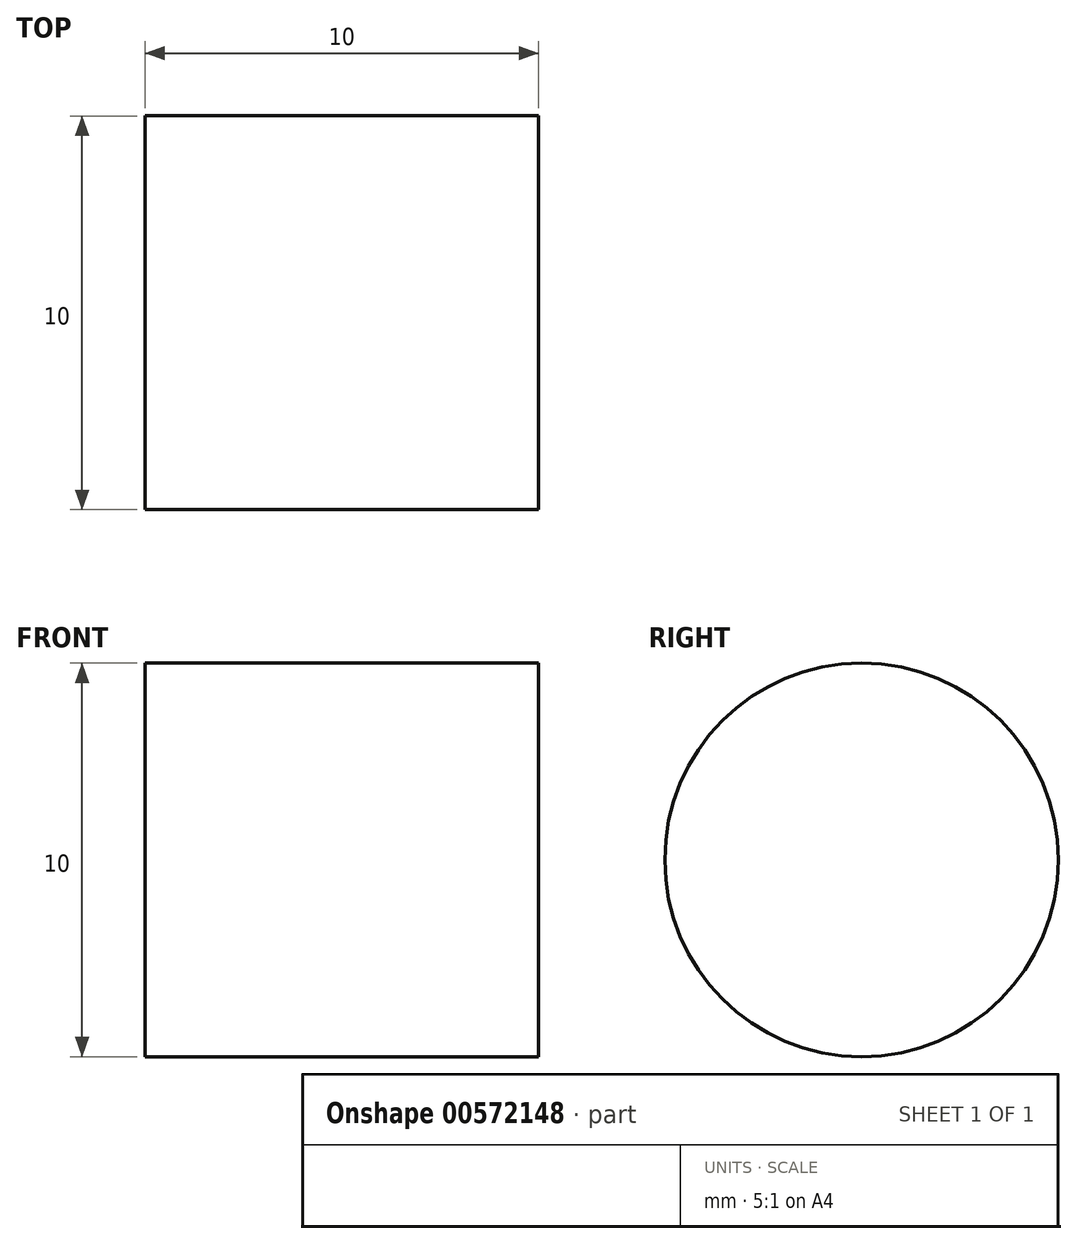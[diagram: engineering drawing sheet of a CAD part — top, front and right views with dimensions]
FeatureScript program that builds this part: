
annotation { "Feature Type Name" : "Feature", "Feature Type Description" : "" }
export const myFeature = defineFeature(function(context is Context, id is Id, definition is map)
    precondition{}
    {
        {
            var Q0;
            Q0=qCreatedBy(makeId("Top.planeOp"),FACE);
            var sketch = newSketch(context, id + "F0", { "sketchPlane" : qUnion([Q0])});
            skLineSegment(sketch, "E0.bottom", {"start": v(-1.65, 3.4) * mm, "end": v(8.35, 3.4) * mm});
            skLineSegment(sketch, "E0.top", {"start": v(-1.65, -6.6) * mm, "end": v(8.35, -6.6) * mm});
            skLineSegment(sketch, "E0.left", {"start": v(-1.65, 3.4) * mm, "end": v(-1.65, -6.6) * mm});
            skLineSegment(sketch, "E0.right", {"start": v(8.35, 3.4) * mm, "end": v(8.35, -6.6) * mm});
            skSolve(sketch);
        }
        {
            var Q0;
            Q0 = qSketchRegion(id + "F0", true);
            extrude(context, id + "F1", {"entities" : qUnion([Q0]), "depth" : 10 * mm, "offsetDistance" : 25 * mm});
        }
        {
            var Q0;
            Q0=makeQuery(id+"F1.opExtrude","CAP_EDGE",EDGE,{"disambiguationData":[OSD([sQuery(id+"F0.wireOp",EDGE,"E0.top")])],"isStart":false});
            var Q1;
            Q1=makeQuery(id+"F1.opExtrude","CAP_EDGE",EDGE,{"disambiguationData":[OSD([sQuery(id+"F0.wireOp",EDGE,"E0.top")])],"isStart":true});
            var Q2;
            Q2=makeQuery(id+"F1.opExtrude","CAP_EDGE",EDGE,{"disambiguationData":[OSD([sQuery(id+"F0.wireOp",EDGE,"E0.bottom")])],"isStart":true});
            var Q3;
            Q3=makeQuery(id+"F1.opExtrude","CAP_EDGE",EDGE,{"disambiguationData":[OSD([sQuery(id+"F0.wireOp",EDGE,"E0.bottom")])],"isStart":false});
            fillet(context, id + "F2", {"entities" : qUnion([Q0, Q1, Q2, Q3]), "tangentPropagation" : true, "radius" : 5 * mm, "defaultsChanged" : false, "vertexSettings" : [], "allowEdgeOverflow" : false});
        }
    });
